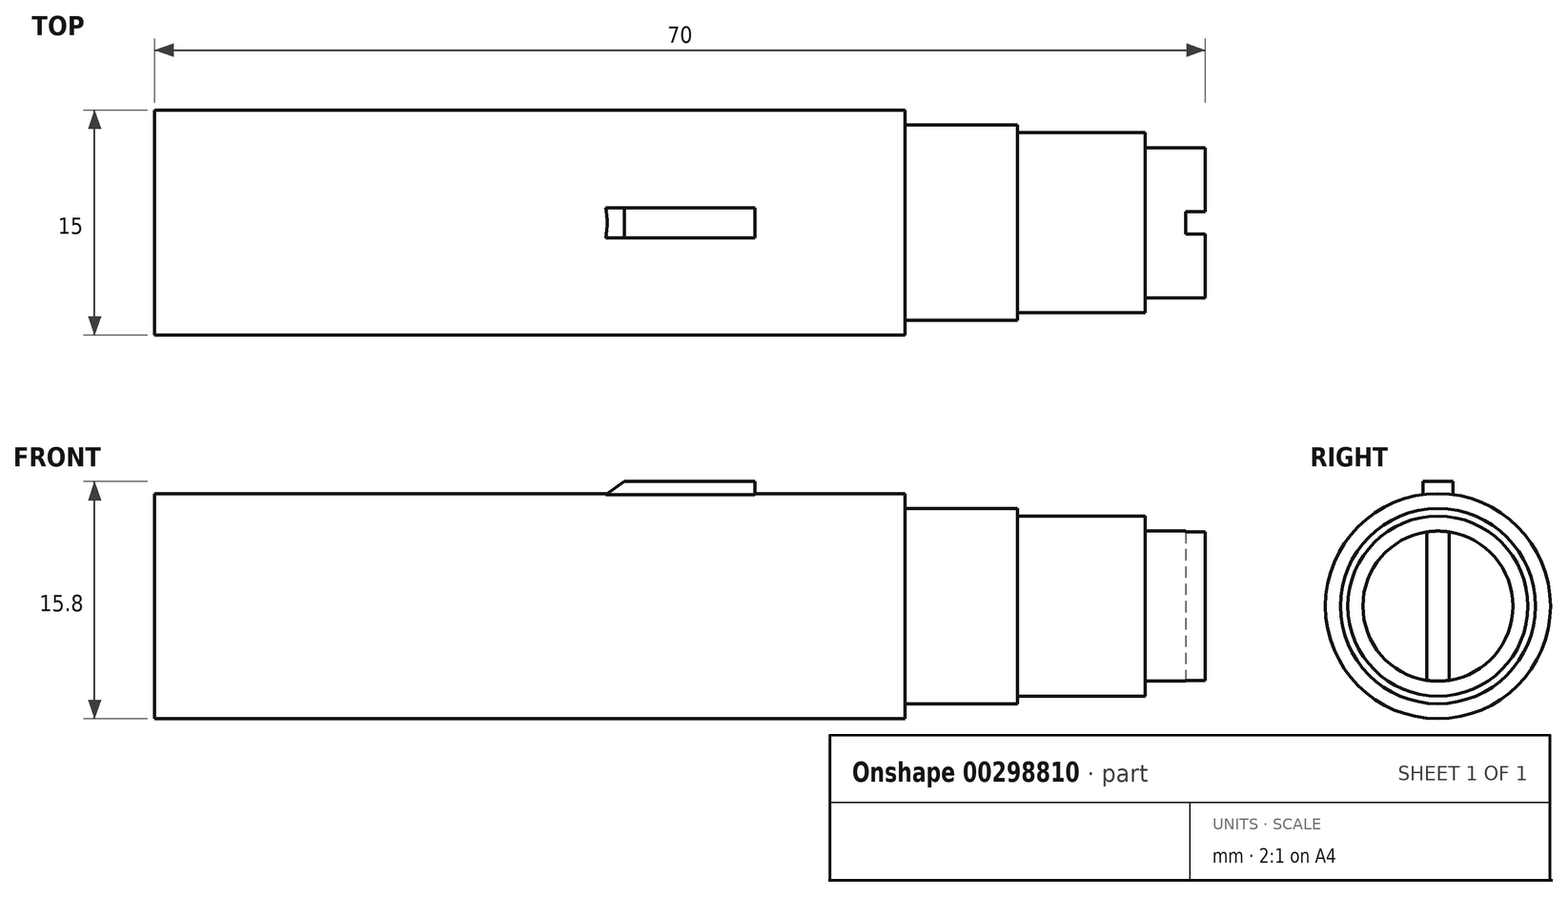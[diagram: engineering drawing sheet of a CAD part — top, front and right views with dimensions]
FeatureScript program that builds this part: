
annotation { "Feature Type Name" : "Feature", "Feature Type Description" : "" }
export const myFeature = defineFeature(function(context is Context, id is Id, definition is map)
    precondition{}
    {
        {
            var Q0;
            Q0=qCreatedBy(makeId("Front.planeOp"),FACE);
            var sketch = newSketch(context, id + "F0", { "sketchPlane" : qUnion([Q0])});
            skLineSegment(sketch, "E0", {"start": v(66, 5) * mm, "end": v(66, 6) * mm});
            skLineSegment(sketch, "E1", {"start": v(66, 5) * mm, "end": v(70, 5) * mm});
            skLineSegment(sketch, "E2", {"start": v(70, 5) * mm, "end": v(70, 0) * mm});
            skLineSegment(sketch, "E3", {"start": v(70, 0) * mm, "end": v(0, 0) * mm});
            skLineSegment(sketch, "E4", {"start": v(0, 0) * mm, "end": v(0, 7.5) * mm});
            skLineSegment(sketch, "E5", {"start": v(-10.7, 0) * mm, "end": v(55.74, 0) * mm, "construction": true});
            skLineSegment(sketch, "E6", {"start": v(66, 6) * mm, "end": v(57.5, 6) * mm});
            skLineSegment(sketch, "E7", {"start": v(57.5, 6.5) * mm, "end": v(57.5, 6) * mm});
            skLineSegment(sketch, "E8", {"start": v(57.5, 6.5) * mm, "end": v(50, 6.5) * mm});
            skLineSegment(sketch, "E9", {"start": v(50, 6.5) * mm, "end": v(50, 7.5) * mm});
            skLineSegment(sketch, "E10", {"start": v(50, 7.5) * mm, "end": v(0, 7.5) * mm});
            skSolve(sketch);
        }
        {
            var Q0;
            Q0=makeQuery(id+"F0.imprint","IMPRINT",FACE,{"disambiguationData":[TD([[makeQuery(id+"F0.imprint","IMPRINT",EDGE,{"derivedFrom":sQuery(id+"F0.wireOp",EDGE,"E0")}),1.0]])]});
            var Q1;
            Q1=sQuery(id+"F0.wireOp",EDGE,"E5");
            revolve(context, id + "F1", {"entities" : qUnion([Q0]), "axis" : qUnion([Q1]), "revolveType" : RevolveType.FULL});
        }
        {
            var Q0;
            Q0=makeQuery(id+"F1.opRevolve","SWEPT_FACE",FACE,{"disambiguationData":[OSD([sQuery(id+"F0.wireOp",EDGE,"E2")])]});
            var sketch = newSketch(context, id + "F2", { "sketchPlane" : qUnion([Q0])});
            skLineSegment(sketch, "E11.left", {"start": v(-0.75, 4.94) * mm, "end": v(-0.75, -4.94) * mm});
            skLineSegment(sketch, "E11.right", {"start": v(0.75, 4.94) * mm, "end": v(0.75, -4.94) * mm});
            skPoint(sketch, "E11.middle", {"position": v(0, 0) * mm});
            skSolve(sketch);
        }
        {
            var Q0;
            Q0=makeQuery(id+"F2.imprint","IMPRINT",FACE,{"disambiguationData":[TD([[makeQuery(id+"F2.imprint","IMPRINT",EDGE,{"derivedFrom":sQuery(id+"F2.wireOp",EDGE,"FBwAMa7p-QO84-0Fqb-Saa4-jfpiWgNZ9to6")}),1.0]])]});
            var Q1;
            Q1=makeQuery(id+"F2.imprint","IMPRINT",FACE,{"disambiguationData":[TD([[makeQuery(id+"F2.imprint","IMPRINT",EDGE,{"derivedFrom":makeQuery(id+"F1.opRevolve","SWEPT_EDGE",EDGE,{"disambiguationData":[OSD([sQuery(id+"F0.wireOp",EDGE,"E1"),sQuery(id+"F0.wireOp",EDGE,"E2")])]})}),-1.0]])]});
            extrude(context, id + "F3", {"entities" : qUnion([Q0, Q1]), "operationType" : NewBodyOperationType.REMOVE, "oppositeDirection" : true, "depth" : 1.3 * mm});
        }
        {
            var Q0;
            Q0=makeQuery(id+"F1.opRevolve","SWEPT_FACE",FACE,{"disambiguationData":[OSD([sQuery(id+"F0.wireOp",EDGE,"E9")])]});
            var sketch = newSketch(context, id + "F4", { "sketchPlane" : qUnion([Q0])});
            skCircle(sketch, "E12", {"center": v(0, 0) * mm, "radius": 7.5 * mm});
            skLineSegment(sketch, "E13", {"start": v(-1, 7.43) * mm, "end": v(-1, 8.3) * mm});
            skLineSegment(sketch, "E14", {"start": v(-1, 8.3) * mm, "end": v(1, 8.3) * mm});
            skLineSegment(sketch, "E15", {"start": v(1, 8.3) * mm, "end": v(1, 7.43) * mm});
            skSolve(sketch);
        }
        {
            var Q0;
            {var subQ0=sQuery(id+"F4.wireOp",EDGE,"E13");Q0=makeQuery(id+"F4.imprint","IMPRINT",FACE,{"disambiguationData":[TD([[makeQuery(id+"F4.imprint","IMPRINT",EDGE,{"derivedFrom":subQ0}),-1.0]])]});}
            extrude(context, id + "F5", {"entities" : qUnion([Q0]), "operationType" : NewBodyOperationType.ADD, "oppositeDirection" : true, "depth" : 20 * mm, "hasSecondDirection" : true, "secondDirectionOppositeDirection" : true, "secondDirectionDepth" : 10 * mm});
        }
        {
            var Q0;
            Q0=makeQuery(id+"F5.opExtrude","CAP_EDGE",EDGE,{"disambiguationData":[OSD([sQuery(id+"F4.wireOp",EDGE,"E14")])],"isStart":false});
            chamfer(context, id + "F6", {"entities" : qUnion([Q0]), "chamferType" : ChamferType.OFFSET_ANGLE, "width" : 0.9 * mm, "oppositeDirection" : false, "angle" : 55 * degree, "tangentPropagation" : true});
        }
    });
